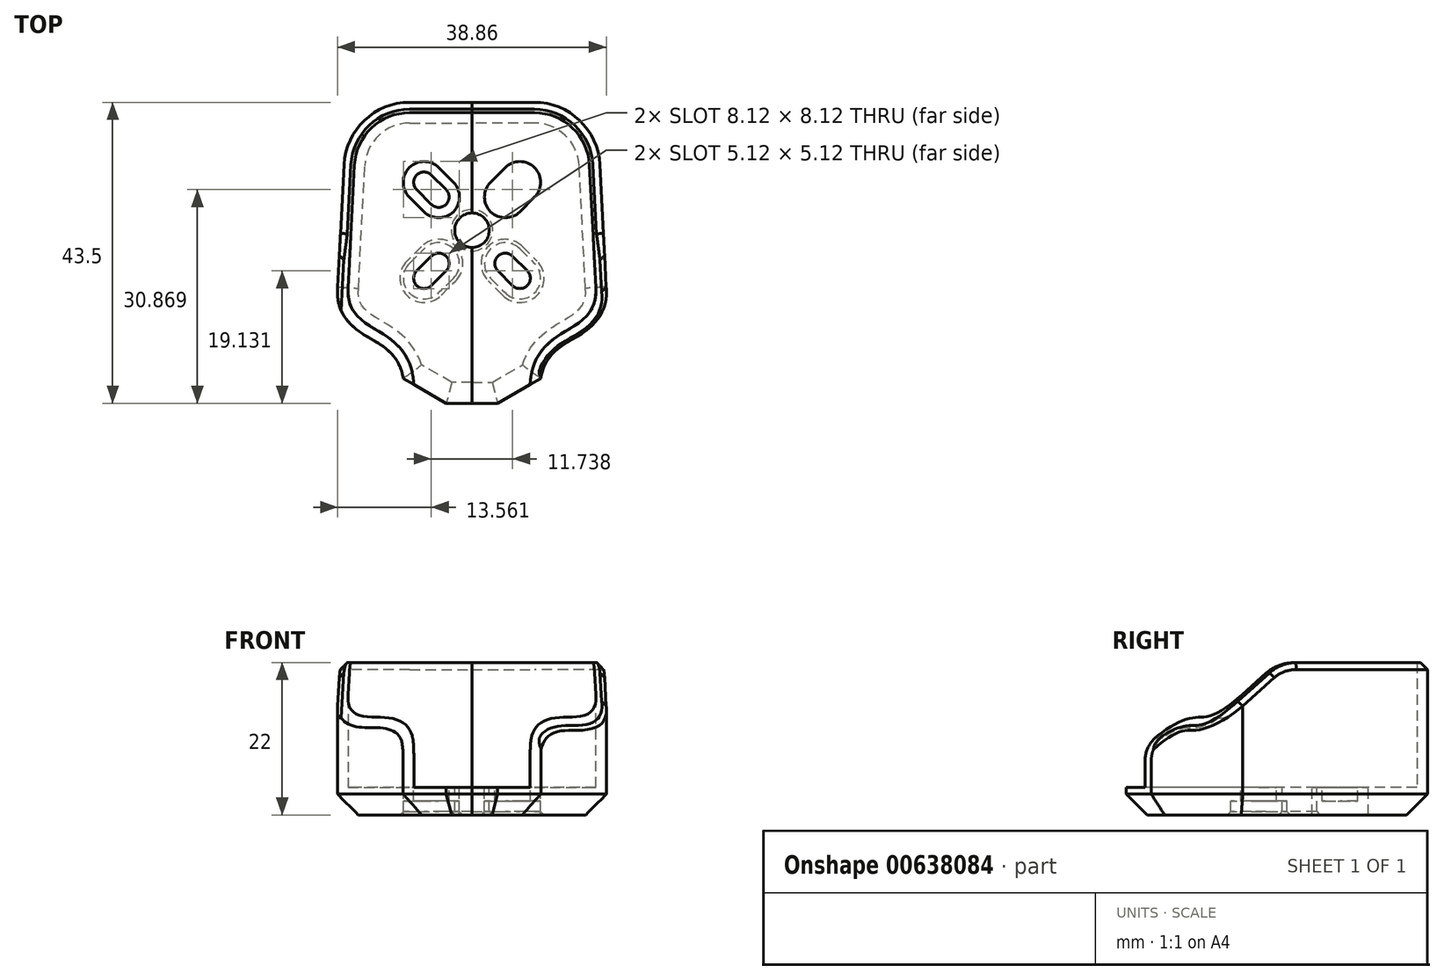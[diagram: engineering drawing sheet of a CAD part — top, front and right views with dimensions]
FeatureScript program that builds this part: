
annotation { "Feature Type Name" : "Feature", "Feature Type Description" : "" }
export const myFeature = defineFeature(function(context is Context, id is Id, definition is map)
    precondition{}
    {
        {
            var Q0;
            Q0=qCreatedBy(makeId("Top.planeOp"),FACE);
            var sketch = newSketch(context, id + "F0", { "sketchPlane" : qUnion([Q0])});
            skLineSegment(sketch, "E0", {"start": v(0, 17) * mm, "end": v(0, -25) * mm});
            skLineSegment(sketch, "E1", {"start": v(0, 17) * mm, "end": v(-9, 17) * mm});
            skLineSegment(sketch, "E2", {"start": v(-17, 9.41) * mm, "end": v(-17.9, -8.3) * mm});
            skFitSpline(sketch, "E3", {"points": [v(-17.9, -8.3) * mm, v(-8.4, -22.3) * mm], "startDerivative": vector(-1.2, -21.96) * mm, "endDerivative": vector(1.72, -27.57) * mm});
            skPoint(sketch, "E4.visualSharp", {"position": v(-16.6, 17) * mm});
            skArc(sketch, "E4.filletArc", {"start": v(-9, 17) * mm, "mid": v(-14.51, 14.8) * mm, "end": v(-17, 9.41) * mm});
            skArc(sketch, "E5", {"start": v(0, 2.5) * mm, "mid": v(-2.5, 0) * mm, "end": v(0, -2.5) * mm});
            skLineSegment(sketch, "E6", {"start": v(0, 0) * mm, "end": v(-8, 8) * mm, "construction": true});
            skArc(sketch, "E7", {"start": v(-8, 8) * mm, "mid": v(-6.93, 8.43) * mm, "end": v(-5.87, 8) * mm});
            skArc(sketch, "E8", {"start": v(-3.75, 3.75) * mm, "mid": v(-3.3, 4.8) * mm, "end": v(-3.75, 5.87) * mm});
            skLineSegment(sketch, "E9", {"start": v(-3.75, 5.87) * mm, "end": v(-5.87, 8) * mm});
            skLineSegment(sketch, "E10", {"start": v(-6.93, 6.93) * mm, "end": v(-5.87, 8) * mm, "construction": true});
            skArc(sketch, "E11.MirrorCS", {"start": v(-8, 8) * mm, "mid": v(-8.43, 6.93) * mm, "end": v(-8, 5.87) * mm});
            skLineSegment(sketch, "E12.MirrorCS", {"start": v(-5.87, 3.75) * mm, "end": v(-8, 5.87) * mm});
            skArc(sketch, "E13.MirrorCS", {"start": v(-3.75, 3.75) * mm, "mid": v(-4.8, 3.3) * mm, "end": v(-5.87, 3.75) * mm});
            skArc(sketch, "E14.MirrorCS", {"start": v(-3.75, -3.75) * mm, "mid": v(-4.8, -3.3) * mm, "end": v(-5.87, -3.75) * mm});
            skArc(sketch, "E15.MirrorCS", {"start": v(-3.75, -3.75) * mm, "mid": v(-3.3, -4.8) * mm, "end": v(-3.75, -5.87) * mm});
            skLineSegment(sketch, "E16.MirrorCS", {"start": v(-3.75, -5.87) * mm, "end": v(-5.87, -8) * mm});
            skLineSegment(sketch, "E17.MirrorCS", {"start": v(-5.87, -3.75) * mm, "end": v(-8, -5.87) * mm});
            skArc(sketch, "E18.MirrorCS", {"start": v(-8, -8) * mm, "mid": v(-8.43, -6.93) * mm, "end": v(-8, -5.87) * mm});
            skArc(sketch, "E19.MirrorCS", {"start": v(-8, -8) * mm, "mid": v(-6.93, -8.43) * mm, "end": v(-5.87, -8) * mm});
            skFitSpline(sketch, "E20.0", {"points": [v(-19.4, -8.21) * mm, v(-19.43, -8.75) * mm, v(-19.4, -9.76) * mm, v(-19.1, -11.13) * mm, v(-18.54, -12.32) * mm, v(-17.8, -13.3) * mm, v(-16.97, -14.1) * mm, v(-15.78, -14.99) * mm, v(-14.27, -15.88) * mm, v(-12.9, -16.75) * mm, v(-11.95, -17.53) * mm, v(-11.33, -18.19) * mm, v(-10.8, -18.94) * mm, v(-10.23, -20.15) * mm, v(-9.96, -21.37) * mm, v(-9.9, -22.4) * mm]});
            skLineSegment(sketch, "E20.1", {"start": v(-18.49, 9.49) * mm, "end": v(-19.4, -8.22) * mm});
            skArc(sketch, "E20.2", {"start": v(-9, 18.5) * mm, "mid": v(-15.54, 15.89) * mm, "end": v(-18.49, 9.49) * mm});
            skLineSegment(sketch, "E20.3", {"start": v(0, 18.5) * mm, "end": v(-9, 18.5) * mm});
            skLineSegment(sketch, "E21", {"start": v(0, 17) * mm, "end": v(0, 18.5) * mm});
            skArc(sketch, "E22", {"start": v(0, -14) * mm, "mid": v(-14, 0) * mm, "end": v(0, 14) * mm, "construction": true});
            skLineSegment(sketch, "E23", {"start": v(-10, -21.37) * mm, "end": v(-3.72, -25) * mm});
            skLineSegment(sketch, "E24", {"start": v(-3.72, -25) * mm, "end": v(0, -25) * mm});
            skArc(sketch, "E25.0", {"start": v(-9.05, 9.05) * mm, "mid": v(-9.93, 6.93) * mm, "end": v(-9.05, 4.8) * mm});
            skLineSegment(sketch, "E25.1", {"start": v(-2.69, 6.93) * mm, "end": v(-4.8, 9.05) * mm});
            skArc(sketch, "E25.2", {"start": v(-2.69, 2.69) * mm, "mid": v(-1.8, 4.8) * mm, "end": v(-2.69, 6.93) * mm});
            skArc(sketch, "E25.3", {"start": v(-9.05, 9.05) * mm, "mid": v(-6.93, 9.93) * mm, "end": v(-4.8, 9.05) * mm});
            skArc(sketch, "E25.4", {"start": v(-2.69, 2.69) * mm, "mid": v(-4.8, 1.8) * mm, "end": v(-6.93, 2.69) * mm});
            skLineSegment(sketch, "E25.5", {"start": v(-6.93, 2.69) * mm, "end": v(-9.05, 4.8) * mm});
            skArc(sketch, "E26.MirrorCS", {"start": v(-9.05, -9.05) * mm, "mid": v(-6.93, -9.93) * mm, "end": v(-4.8, -9.05) * mm});
            skArc(sketch, "E27.MirrorCS", {"start": v(-9.05, -9.05) * mm, "mid": v(-9.93, -6.93) * mm, "end": v(-9.05, -4.8) * mm});
            skLineSegment(sketch, "E28.MirrorCS", {"start": v(-6.93, -2.69) * mm, "end": v(-9.05, -4.8) * mm});
            skArc(sketch, "E29.MirrorCS", {"start": v(-2.69, -2.69) * mm, "mid": v(-4.8, -1.8) * mm, "end": v(-6.93, -2.69) * mm});
            skArc(sketch, "E30.MirrorCS", {"start": v(-2.69, -2.69) * mm, "mid": v(-1.8, -4.8) * mm, "end": v(-2.69, -6.93) * mm});
            skLineSegment(sketch, "E31.MirrorCS", {"start": v(-2.69, -6.93) * mm, "end": v(-4.8, -9.05) * mm});
            skSolve(sketch);
        }
        {
            var Q0;
            {var subQ2=sQuery(id+"F0.wireOp",EDGE,"E1");Q0=makeQuery(id+"F0.imprint","IMPRINT",FACE,{"disambiguationData":[TD([[makeQuery(id+"F0.imprint","IMPRINT",EDGE,{"derivedFrom":subQ2}),1.0]])]});}
            var Q1;
            Q1=makeQuery(id+"F0.imprint","IMPRINT",FACE,{"disambiguationData":[TD([[makeQuery(id+"F0.imprint","IMPRINT",EDGE,{"derivedFrom":sQuery(id+"F0.wireOp",EDGE,"E1")}),-1.0]])]});
            var Q2;
            Q2=makeQuery(id+"F0.imprint","IMPRINT",FACE,{"disambiguationData":[TD([[makeQuery(id+"F0.imprint","IMPRINT",EDGE,{"derivedFrom":sQuery(id+"F0.wireOp",EDGE,"E7")}),1.0]])]});
            var Q3;
            Q3=makeQuery(id+"F0.imprint","IMPRINT",FACE,{"disambiguationData":[TD([[makeQuery(id+"F0.imprint","IMPRINT",EDGE,{"derivedFrom":sQuery(id+"F0.wireOp",EDGE,"E14.MirrorCS")}),-1.0]])]});
            extrude(context, id + "F1", {"entities" : qUnion([Q0, Q1, Q2, Q3]), "oppositeDirection" : true, "depth" : 4 * mm, "offsetDistance" : 25 * mm});
        }
        {
            var Q0;
            Q0=makeQuery(id+"F0.imprint","IMPRINT",FACE,{"disambiguationData":[TD([[makeQuery(id+"F0.imprint","IMPRINT",EDGE,{"derivedFrom":sQuery(id+"F0.wireOp",EDGE,"E1")}),-1.0]])]});
            extrude(context, id + "F2", {"entities" : qUnion([Q0]), "operationType" : NewBodyOperationType.ADD, "depth" : 18 * mm, "offsetDistance" : 25 * mm});
        }
        {
            var Q0;
            Q0=makeQuery(id+"F0.imprint","IMPRINT",FACE,{"disambiguationData":[TD([[makeQuery(id+"F0.imprint","IMPRINT",EDGE,{"derivedFrom":sQuery(id+"F0.wireOp",EDGE,"E14.MirrorCS")}),-1.0]])]});
            var Q1;
            Q1=makeQuery(id+"F0.imprint","IMPRINT",FACE,{"disambiguationData":[TD([[makeQuery(id+"F0.imprint","IMPRINT",EDGE,{"derivedFrom":sQuery(id+"F0.wireOp",EDGE,"E7")}),1.0]])]});
            extrude(context, id + "F3", {"entities" : qUnion([Q0, Q1]), "operationType" : NewBodyOperationType.REMOVE, "endBound" : BoundingType.THROUGH_ALL, "oppositeDirection" : true, "depth" : 25 * mm, "offsetDistance" : 25 * mm, "hasSecondDirection" : true, "secondDirectionOppositeDirection" : true, "secondDirectionDepth" : 2 * mm});
        }
        {
            var Q0;
            Q0=makeQuery(id+"F1.opExtrude","CAP_EDGE",EDGE,{"disambiguationData":[OSD([sQuery(id+"F0.wireOp",EDGE,"E20.0")])],"isStart":false});
            var Q1;
            Q1=makeQuery(id+"F1.opExtrude","CAP_EDGE",EDGE,{"disambiguationData":[OSD([sQuery(id+"F0.wireOp",EDGE,"E20.2")])],"isStart":false});
            var Q2;
            Q2=makeQuery(id+"F1.opExtrude","CAP_EDGE",EDGE,{"disambiguationData":[OSD([sQuery(id+"F0.wireOp",EDGE,"QeRF42VJ-7esz-RBey-jn3b-T6qpRaJM10pB"),sQuery(id+"F0.wireOp",EDGE,"5uH67odv-xHYW-Wwju-5o4u-S0CyTWI5CNgH")])],"isStart":false});
            var Q3;
            Q3=makeQuery(id+"F1.opExtrude","CAP_EDGE",EDGE,{"disambiguationData":[OSD([sQuery(id+"F0.wireOp",EDGE,"E23")])],"isStart":false});
            var Q4;
            Q4=makeQuery(id+"F1.opExtrude","CAP_EDGE",EDGE,{"disambiguationData":[OSD([sQuery(id+"F0.wireOp",EDGE,"E24")])],"isStart":false});
            chamfer(context, id + "F4", {"entities" : qUnion([Q0, Q1, Q2, Q3, Q4]), "width" : 3 * mm, "tangentPropagation" : true});
        }
        {
            var Q0;
            Q0=makeQuery(id+"F2.opExtrude","CAP_EDGE",EDGE,{"disambiguationData":[OSD([sQuery(id+"F0.wireOp",EDGE,"E23")])],"isStart":false});
            chamfer(context, id + "F5", {"entities" : qUnion([Q0]), "width" : 12 * mm, "tangentPropagation" : true});
        }
        {
            var Q0;
            {var subQ0=sQuery(id+"F0.wireOp",EDGE,"E23");Q0=makeQuery(id+"F5.opChamfer","BLEND_EDGE",EDGE,{"blendedFrom":[makeQuery(id+"F2.opExtrude","CAP_EDGE",EDGE,{"disambiguationData":[OSD([subQ0])],"isStart":false}),makeQuery(id+"F2.boolean.opBoolean","MERGE",FACE,{"derivedFrom":[makeQuery(id+"F1.opExtrude","SWEPT_FACE",FACE,{"disambiguationData":[OSD([subQ0])]}),makeQuery(id+"F2.opExtrude","SWEPT_FACE",FACE,{"disambiguationData":[OSD([subQ0])]})]})],"blendedInto":[makeQuery(id+"F2.boolean.opBoolean","MERGE",FACE,{"derivedFrom":[makeQuery(id+"F1.opExtrude","SWEPT_FACE",FACE,{"disambiguationData":[OSD([subQ0])]}),makeQuery(id+"F2.opExtrude","SWEPT_FACE",FACE,{"disambiguationData":[OSD([subQ0])]})]})]});}
            var Q1;
            {var subQ0=sQuery(id+"F0.wireOp",EDGE,"E23");Q1=makeQuery(id+"F5.opChamfer","BLEND_EDGE",EDGE,{"blendedFrom":[makeQuery(id+"F2.opExtrude","CAP_EDGE",EDGE,{"disambiguationData":[OSD([subQ0])],"isStart":false}),makeQuery(id+"F2.opExtrude","CAP_FACE",FACE,{"disambiguationData":[OSD([sQuery(id+"F0.wireOp",EDGE,"E1"),sQuery(id+"F0.wireOp",EDGE,"E2"),sQuery(id+"F0.wireOp",EDGE,"E3"),sQuery(id+"F0.wireOp",EDGE,"E4.filletArc"),sQuery(id+"F0.wireOp",EDGE,"E20.0"),sQuery(id+"F0.wireOp",EDGE,"E20.1"),sQuery(id+"F0.wireOp",EDGE,"E20.2"),sQuery(id+"F0.wireOp",EDGE,"E20.3"),sQuery(id+"F0.wireOp",EDGE,"E21"),subQ0])],"isStart":false})],"blendedInto":[makeQuery(id+"F2.opExtrude","CAP_FACE",FACE,{"disambiguationData":[OSD([sQuery(id+"F0.wireOp",EDGE,"E1"),sQuery(id+"F0.wireOp",EDGE,"E2"),sQuery(id+"F0.wireOp",EDGE,"E3"),sQuery(id+"F0.wireOp",EDGE,"E4.filletArc"),sQuery(id+"F0.wireOp",EDGE,"E20.0"),sQuery(id+"F0.wireOp",EDGE,"E20.1"),sQuery(id+"F0.wireOp",EDGE,"E20.2"),sQuery(id+"F0.wireOp",EDGE,"E20.3"),sQuery(id+"F0.wireOp",EDGE,"E21"),subQ0])],"isStart":false})]});}
            fillet(context, id + "F6", {"entities" : qUnion([Q0, Q1]), "radius" : 5 * mm, "tangentPropagation" : true, "allowEdgeOverflow" : false});
        }
        {
            var Q0;
            Q0=makeQuery(id+"F3.boolean.opBoolean","INTERSECT",EDGE,{"derivedFrom":[makeQuery(id+"F1.opExtrude","CAP_FACE",FACE,{"disambiguationData":[OSD([sQuery(id+"F0.wireOp",EDGE,"E0"),sQuery(id+"F0.wireOp",EDGE,"E5"),sQuery(id+"F0.wireOp",EDGE,"E7"),sQuery(id+"F0.wireOp",EDGE,"E8"),sQuery(id+"F0.wireOp",EDGE,"E9"),sQuery(id+"F0.wireOp",EDGE,"E11.MirrorCS"),sQuery(id+"F0.wireOp",EDGE,"E12.MirrorCS"),sQuery(id+"F0.wireOp",EDGE,"E13.MirrorCS"),sQuery(id+"F0.wireOp",EDGE,"E14.MirrorCS"),sQuery(id+"F0.wireOp",EDGE,"E15.MirrorCS"),sQuery(id+"F0.wireOp",EDGE,"E16.MirrorCS"),sQuery(id+"F0.wireOp",EDGE,"E17.MirrorCS"),sQuery(id+"F0.wireOp",EDGE,"E18.MirrorCS"),sQuery(id+"F0.wireOp",EDGE,"E19.MirrorCS"),sQuery(id+"F0.wireOp",EDGE,"E20.0"),sQuery(id+"F0.wireOp",EDGE,"E20.1"),sQuery(id+"F0.wireOp",EDGE,"E20.2"),sQuery(id+"F0.wireOp",EDGE,"E20.3"),sQuery(id+"F0.wireOp",EDGE,"E21"),sQuery(id+"F0.wireOp",EDGE,"E23"),sQuery(id+"F0.wireOp",EDGE,"E24")])],"isStart":false}),makeQuery(id+"F3.opExtrude","SWEPT_FACE",FACE,{"disambiguationData":[OSD([sQuery(id+"F0.wireOp",EDGE,"E26.MirrorCS"),sQuery(id+"F0.wireOp",EDGE,"E27.MirrorCS")])]})]});
            var Q1;
            Q1=makeQuery(id+"F3.boolean.opBoolean","INTERSECT",EDGE,{"derivedFrom":[makeQuery(id+"F1.opExtrude","CAP_FACE",FACE,{"disambiguationData":[OSD([sQuery(id+"F0.wireOp",EDGE,"E0"),sQuery(id+"F0.wireOp",EDGE,"E5"),sQuery(id+"F0.wireOp",EDGE,"E7"),sQuery(id+"F0.wireOp",EDGE,"E8"),sQuery(id+"F0.wireOp",EDGE,"E9"),sQuery(id+"F0.wireOp",EDGE,"E11.MirrorCS"),sQuery(id+"F0.wireOp",EDGE,"E12.MirrorCS"),sQuery(id+"F0.wireOp",EDGE,"E13.MirrorCS"),sQuery(id+"F0.wireOp",EDGE,"E14.MirrorCS"),sQuery(id+"F0.wireOp",EDGE,"E15.MirrorCS"),sQuery(id+"F0.wireOp",EDGE,"E16.MirrorCS"),sQuery(id+"F0.wireOp",EDGE,"E17.MirrorCS"),sQuery(id+"F0.wireOp",EDGE,"E18.MirrorCS"),sQuery(id+"F0.wireOp",EDGE,"E19.MirrorCS"),sQuery(id+"F0.wireOp",EDGE,"E20.0"),sQuery(id+"F0.wireOp",EDGE,"E20.1"),sQuery(id+"F0.wireOp",EDGE,"E20.2"),sQuery(id+"F0.wireOp",EDGE,"E20.3"),sQuery(id+"F0.wireOp",EDGE,"E21"),sQuery(id+"F0.wireOp",EDGE,"E23"),sQuery(id+"F0.wireOp",EDGE,"E24")])],"isStart":false}),makeQuery(id+"F3.opExtrude","SWEPT_FACE",FACE,{"disambiguationData":[OSD([sQuery(id+"F0.wireOp",EDGE,"E25.0"),sQuery(id+"F0.wireOp",EDGE,"E25.3")])]})]});
            var Q2;
            Q2=makeQuery(id+"F1.opExtrude","CAP_EDGE",EDGE,{"disambiguationData":[OSD([sQuery(id+"F0.wireOp",EDGE,"E5")])],"isStart":false});
            chamfer(context, id + "F7", {"entities" : qUnion([Q0, Q1, Q2]), "width" : 0.5 * mm, "tangentPropagation" : true});
        }
        {
            var Q0;
            Q0=makeQuery(id+"F1.opExtrude","SWEPT_BODY",BODY,{"disambiguationData":[OSD([sQuery(id+"F0.wireOp",EDGE,"E0"),sQuery(id+"F0.wireOp",EDGE,"E5"),sQuery(id+"F0.wireOp",EDGE,"E7"),sQuery(id+"F0.wireOp",EDGE,"E8"),sQuery(id+"F0.wireOp",EDGE,"E9"),sQuery(id+"F0.wireOp",EDGE,"E11.MirrorCS"),sQuery(id+"F0.wireOp",EDGE,"E12.MirrorCS"),sQuery(id+"F0.wireOp",EDGE,"E13.MirrorCS"),sQuery(id+"F0.wireOp",EDGE,"E14.MirrorCS"),sQuery(id+"F0.wireOp",EDGE,"E15.MirrorCS"),sQuery(id+"F0.wireOp",EDGE,"E16.MirrorCS"),sQuery(id+"F0.wireOp",EDGE,"E17.MirrorCS"),sQuery(id+"F0.wireOp",EDGE,"E18.MirrorCS"),sQuery(id+"F0.wireOp",EDGE,"E19.MirrorCS"),sQuery(id+"F0.wireOp",EDGE,"E20.0"),sQuery(id+"F0.wireOp",EDGE,"E20.1"),sQuery(id+"F0.wireOp",EDGE,"E20.2"),sQuery(id+"F0.wireOp",EDGE,"E20.3"),sQuery(id+"F0.wireOp",EDGE,"E21"),sQuery(id+"F0.wireOp",EDGE,"E23"),sQuery(id+"F0.wireOp",EDGE,"E24")])]});
            var Q1;
            Q1=qCreatedBy(makeId("Right.planeOp"),FACE);
            mirror(context, id + "F8", {"operationType" : NewBodyOperationType.ADD, "entities" : qUnion([Q0]), "mirrorPlane" : qUnion([Q1])});
        }
        {
            var Q0;
            {var subQ0=makeQuery(id+"F2.opExtrude","CAP_EDGE",EDGE,{"disambiguationData":[OSD([sQuery(id+"F0.wireOp",EDGE,"E20.3")])],"isStart":false});Q0=makeQuery(id+"F8.boolean.opBoolean","MERGE",EDGE,{"derivedFrom":[subQ0,makeQuery(id+"F8.opPattern","COPY",EDGE,{"derivedFrom":subQ0,"instanceName":"1"})]});}
            chamfer(context, id + "F9", {"entities" : qUnion([Q0]), "width" : 1 * mm, "tangentPropagation" : true});
        }
    });
